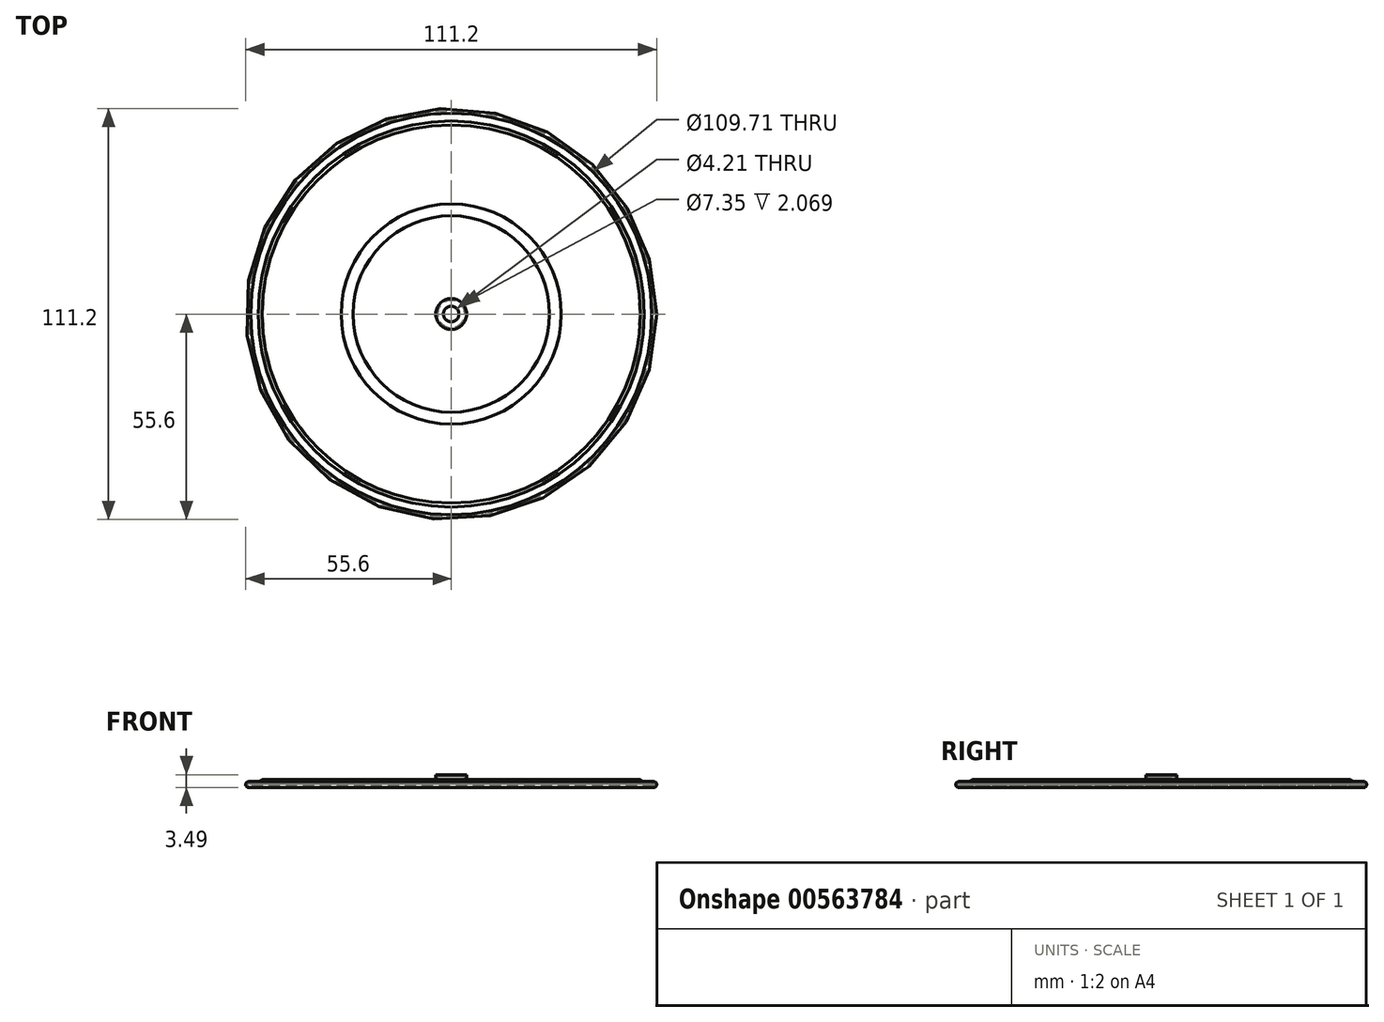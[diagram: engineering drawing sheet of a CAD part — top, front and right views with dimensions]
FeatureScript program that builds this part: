
annotation { "Feature Type Name" : "Feature", "Feature Type Description" : "" }
export const myFeature = defineFeature(function(context is Context, id is Id, definition is map)
    precondition{}
    {
        {
            var Q0;
            Q0=qCreatedBy(makeId("Front.planeOp"),FACE);
            var sketch = newSketch(context, id + "F0", { "sketchPlane" : qUnion([Q0])});
            skArc(sketch, "E0", {"start": v(54.86, 10.9) * mm, "mid": v(55.02, 11.39) * mm, "end": v(54.52, 11.31) * mm});
            skLineSegment(sketch, "E1", {"start": v(3.67, 13.38) * mm, "end": v(3.67, 11.3) * mm});
            skLineSegment(sketch, "E2", {"start": v(3.67, 11.3) * mm, "end": v(26.62, 11.3) * mm});
            skLineSegment(sketch, "E3", {"start": v(26.62, 11.3) * mm, "end": v(29.83, 12.01) * mm});
            skLineSegment(sketch, "E4", {"start": v(29.83, 12.01) * mm, "end": v(51, 12.01) * mm});
            skLineSegment(sketch, "E5", {"start": v(51, 12.01) * mm, "end": v(52.05, 11.3) * mm});
            skLineSegment(sketch, "E6", {"start": v(52.05, 11.3) * mm, "end": v(54.52, 11.31) * mm});
            skLineSegment(sketch, "E7", {"start": v(3.67, 13.38) * mm, "end": v(2.1, 13.38) * mm});
            skLineSegment(sketch, "E8.0", {"start": v(4.18, 13.88) * mm, "end": v(2.1, 13.88) * mm});
            skLineSegment(sketch, "E8.1", {"start": v(4.18, 13.88) * mm, "end": v(4.18, 11.82) * mm});
            skLineSegment(sketch, "E8.2", {"start": v(4.18, 11.82) * mm, "end": v(26.57, 11.82) * mm});
            skLineSegment(sketch, "E8.3", {"start": v(52.2, 11.82) * mm, "end": v(54.26, 11.82) * mm});
            skLineSegment(sketch, "E8.4", {"start": v(51.16, 12.52) * mm, "end": v(52.2, 11.82) * mm});
            skLineSegment(sketch, "E8.5", {"start": v(29.77, 12.52) * mm, "end": v(51.16, 12.52) * mm});
            skLineSegment(sketch, "E8.6", {"start": v(26.57, 11.82) * mm, "end": v(29.77, 12.52) * mm});
            skLineSegment(sketch, "E9", {"start": v(54.86, 10.9) * mm, "end": v(54.86, 10.4) * mm});
            skArc(sketch, "E10", {"start": v(54.86, 10.4) * mm, "mid": v(55.54, 11.52) * mm, "end": v(54.26, 11.82) * mm});
            skLineSegment(sketch, "E11", {"start": v(2.1, 13.88) * mm, "end": v(2.1, 13.38) * mm});
            skLineSegment(sketch, "E12", {"start": v(0, 13.88) * mm, "end": v(0, 13.38) * mm});
            skSolve(sketch);
        }
        {
            var Q0;
            Q0=makeQuery(id+"F0.imprint","IMPRINT",FACE,{"disambiguationData":[TD([[makeQuery(id+"F0.imprint","IMPRINT",EDGE,{"derivedFrom":sQuery(id+"F0.wireOp",EDGE,"E0")}),-1.0]])]});
            var Q1;
            Q1=sQuery(id+"F0.wireOp",EDGE,"E12");
            revolve(context, id + "F1", {"entities" : qUnion([Q0]), "axis" : qUnion([Q1]), "revolveType" : RevolveType.FULL});
        }
    });
